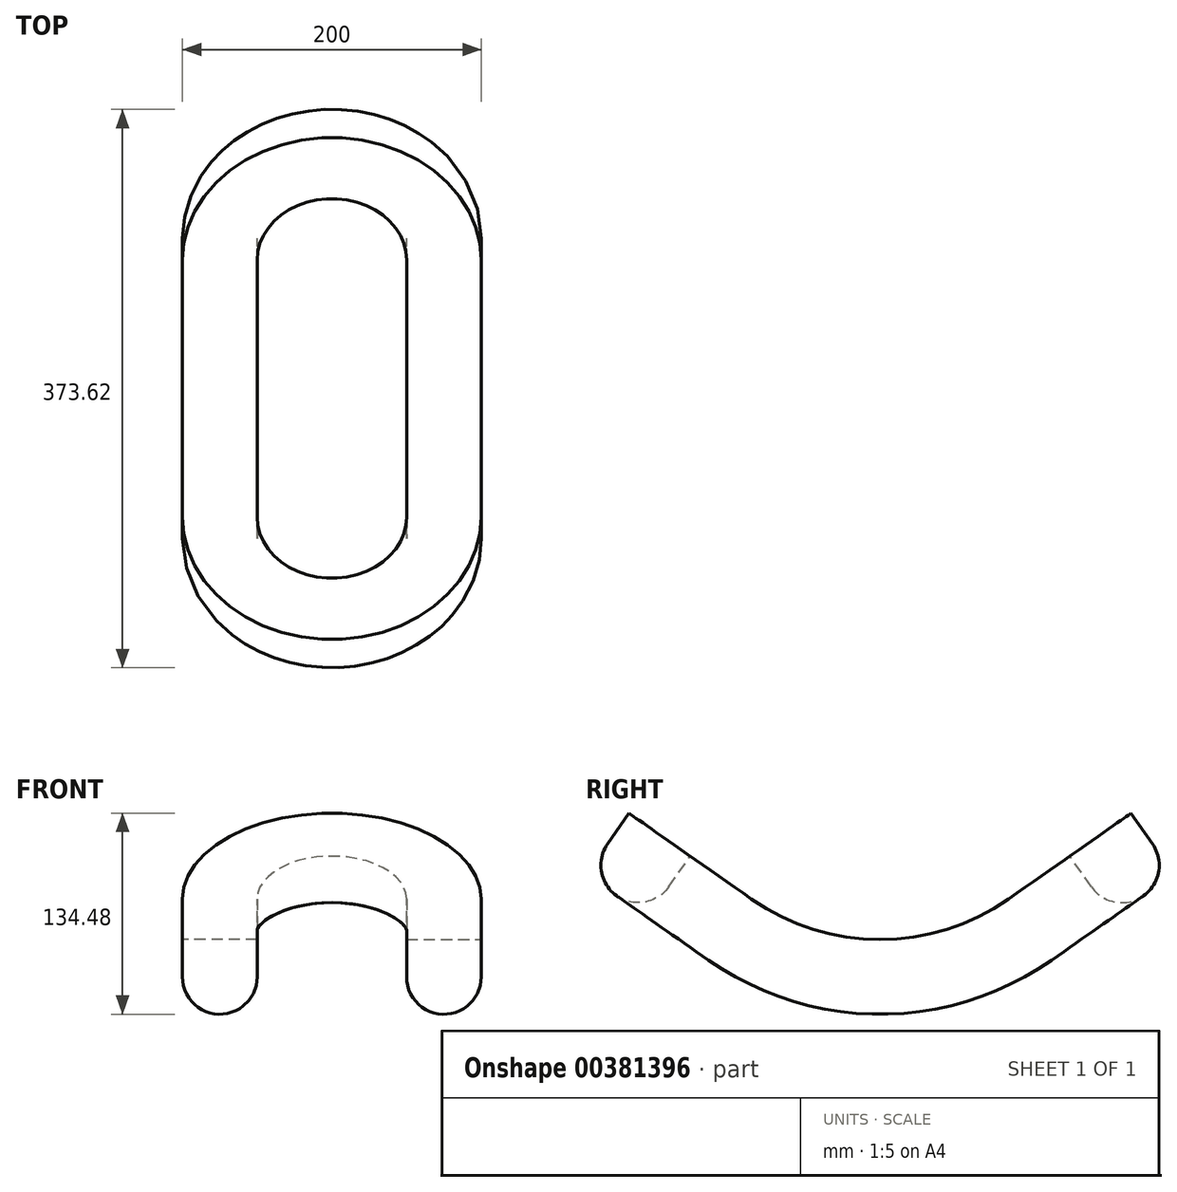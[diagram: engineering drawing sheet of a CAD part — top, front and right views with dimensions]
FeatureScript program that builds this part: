
annotation { "Feature Type Name" : "Feature", "Feature Type Description" : "" }
export const myFeature = defineFeature(function(context is Context, id is Id, definition is map)
    precondition{}
    {
        {
            var Q0;
            Q0=qCreatedBy(makeId("Right.planeOp"),FACE);
            var sketch = newSketch(context, id + "F0", { "sketchPlane" : qUnion([Q0])});
            skArc(sketch, "E0", {"start": v(0, 0) * mm, "mid": v(45.1, 6.94) * mm, "end": v(86.04, 27.13) * mm});
            skLineSegment(sketch, "E1", {"start": v(86.04, 27.13) * mm, "end": v(167.95, 84.48) * mm});
            skLineSegment(sketch, "E2", {"start": v(0, 150) * mm, "end": v(86.04, 27.13) * mm, "construction": true});
            skSolve(sketch);
        }
        {
            var Q0;
            Q0=sQuery(id+"F0.wireOp",EDGE,"E1");
            var Q1;
            Q1=sQuery(id+"F0.wireOp",EDGE,"E0");
            extrude(context, id + "F1", {"bodyType" : ToolBodyType.SURFACE, "surfaceEntities" : qUnion([Q0, Q1]), "depth" : 100 * mm});
        }
        {
            var Q0;
            Q0=makeQuery(id+"F1.opExtrude","SWEPT_FACE",FACE,{"disambiguationData":[OSD([sQuery(id+"F0.wireOp",EDGE,"E1")])]});
            var sketch = newSketch(context, id + "F2", { "sketchPlane" : qUnion([Q0])});
            skArc(sketch, "E3", {"start": v(0, -186.04) * mm, "mid": v(70.71, -156.75) * mm, "end": v(100, -86.04) * mm});
            skSolve(sketch);
        }
        {
            var Q0;
            Q0=qCreatedBy(makeId("Front.planeOp"),FACE);
            var sketch = newSketch(context, id + "F3", { "sketchPlane" : qUnion([Q0])});
            skLineSegment(sketch, "E4.bottom", {"start": v(100, 0) * mm, "end": v(50, 0) * mm});
            skLineSegment(sketch, "E4.top", {"start": v(100, -25) * mm, "end": v(50, -25) * mm, "construction": true});
            skLineSegment(sketch, "E4.left", {"start": v(100, 0) * mm, "end": v(100, -25) * mm});
            skLineSegment(sketch, "E4.right", {"start": v(50, 0) * mm, "end": v(50, -25) * mm});
            skArc(sketch, "E5", {"start": v(50, -25) * mm, "mid": v(75, -50) * mm, "end": v(100, -25) * mm});
            skSolve(sketch);
        }
        {
            var Q0;
            Q0=makeQuery(id+"F3.imprint","IMPRINT",FACE,{"disambiguationData":[TD([[makeQuery(id+"F3.imprint","IMPRINT",EDGE,{"derivedFrom":sQuery(id+"F3.wireOp",EDGE,"E4.bottom")}),1.0]])]});
            var Q1;
            Q1=makeQuery(id+"F1.opExtrude","CAP_EDGE",EDGE,{"disambiguationData":[OSD([sQuery(id+"F0.wireOp",EDGE,"E0")])],"isStart":false});
            var Q2;
            Q2=sQuery(id+"F2.wireOp",EDGE,"E3");
            sweep(context, id + "F4", {"profiles" : qUnion([Q0]), "path" : qUnion([Q1, Q2])});
        }
        {
            var Q0;
            Q0=makeQuery(id+"F4.opSweep","SWEPT_BODY",BODY,{"disambiguationData":[OSD([sQuery(id+"F2.wireOp",EDGE,"E3"),sQuery(id+"F3.wireOp",EDGE,"E4.bottom"),sQuery(id+"F3.wireOp",EDGE,"E4.left"),sQuery(id+"F3.wireOp",EDGE,"E4.right"),sQuery(id+"F3.wireOp",EDGE,"E5")])]});
            var Q1;
            Q1=qCreatedBy(makeId("Right.planeOp"),FACE);
            mirror(context, id + "F5", {"operationType" : NewBodyOperationType.ADD, "entities" : qUnion([Q0]), "mirrorPlane" : qUnion([Q1])});
        }
        {
            var Q0;
            Q0=makeQuery(id+"F4.opSweep","SWEPT_BODY",BODY,{"disambiguationData":[OSD([sQuery(id+"F2.wireOp",EDGE,"E3"),sQuery(id+"F3.wireOp",EDGE,"E4.bottom"),sQuery(id+"F3.wireOp",EDGE,"E4.left"),sQuery(id+"F3.wireOp",EDGE,"E4.right"),sQuery(id+"F3.wireOp",EDGE,"E5")])]});
            var Q1;
            Q1=qCreatedBy(makeId("Front.planeOp"),FACE);
            mirror(context, id + "F6", {"operationType" : NewBodyOperationType.ADD, "entities" : qUnion([Q0]), "mirrorPlane" : qUnion([Q1])});
        }
    });
